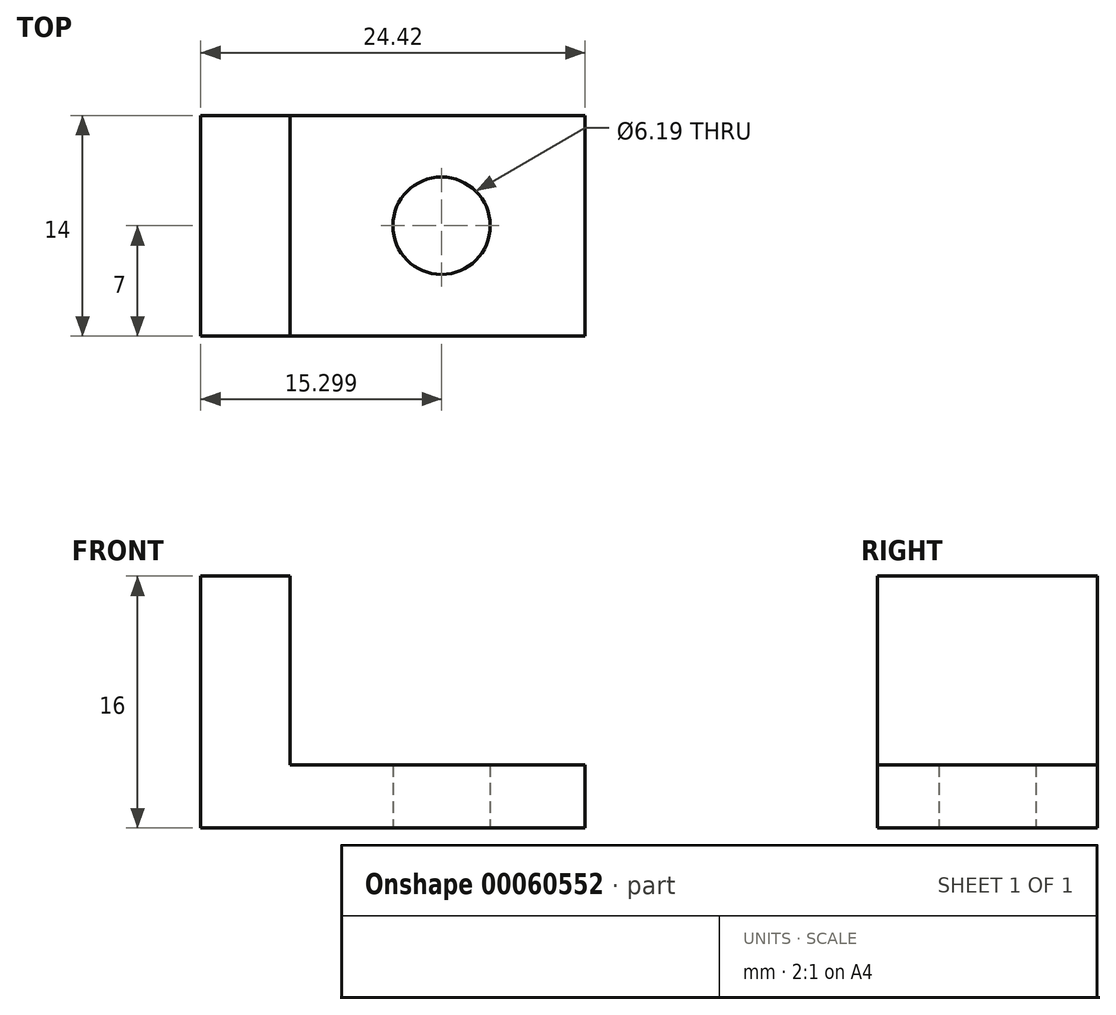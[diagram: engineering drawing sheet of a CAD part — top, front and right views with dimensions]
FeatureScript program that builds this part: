
annotation { "Feature Type Name" : "Feature", "Feature Type Description" : "" }
export const myFeature = defineFeature(function(context is Context, id is Id, definition is map)
    precondition{}
    {
        {
            var Q0;
            Q0=qCreatedBy(makeId("Top.planeOp"),FACE);
            var sketch = newSketch(context, id + "F0", { "sketchPlane" : qUnion([Q0])});
            skLineSegment(sketch, "E0.bottom", {"start": v(2.3, 2.75) * mm, "end": v(-22.11, 2.75) * mm});
            skLineSegment(sketch, "E0.top", {"start": v(2.3, 16.75) * mm, "end": v(-22.11, 16.75) * mm});
            skLineSegment(sketch, "E0.left", {"start": v(2.3, 2.75) * mm, "end": v(2.3, 16.75) * mm});
            skLineSegment(sketch, "E0.right", {"start": v(-22.11, 2.75) * mm, "end": v(-22.11, 16.75) * mm});
            skPoint(sketch, "E0.middle", {"position": v(-9.9, 9.75) * mm});
            skLineSegment(sketch, "E1", {"start": v(-16.42, 16.75) * mm, "end": v(-16.42, 2.75) * mm});
            skCircle(sketch, "E2", {"center": v(-6.81, 9.75) * mm, "radius": 3.1 * mm});
            skSolve(sketch);
        }
        {
            var Q0;
            {var subQ0=sQuery(id+"F0.wireOp",EDGE,"E0.right");Q0=makeQuery(id+"F0.imprint","IMPRINT",FACE,{"disambiguationData":[TD([[makeQuery(id+"F0.imprint","IMPRINT",EDGE,{"derivedFrom":subQ0}),-1.0]])]});}
            extrude(context, id + "F1", {"entities" : qUnion([Q0]), "depth" : 16 * mm});
        }
        {
            var Q0;
            {var subQ1=sQuery(id+"F0.wireOp",EDGE,"E0.left");Q0=makeQuery(id+"F0.imprint","IMPRINT",FACE,{"disambiguationData":[TD([[makeQuery(id+"F0.imprint","IMPRINT",EDGE,{"derivedFrom":subQ1}),1.0]])]});}
            extrude(context, id + "F2", {"entities" : qUnion([Q0]), "operationType" : NewBodyOperationType.ADD, "depth" : 4 * mm});
        }
    });
